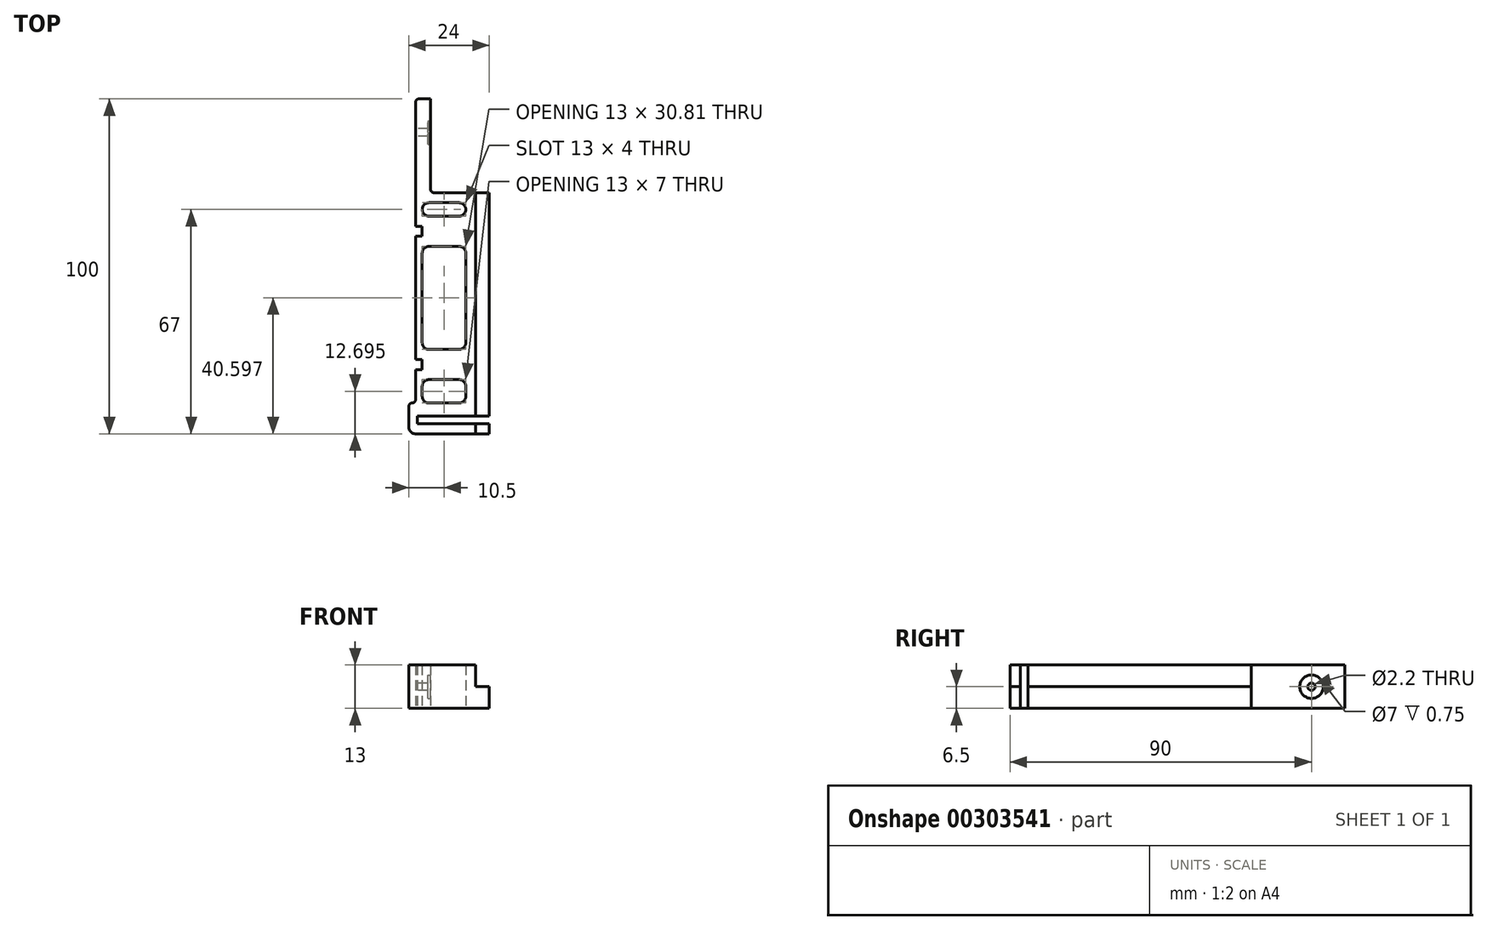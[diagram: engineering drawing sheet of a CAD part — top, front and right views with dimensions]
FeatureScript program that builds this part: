
annotation { "Feature Type Name" : "Feature", "Feature Type Description" : "" }
export const myFeature = defineFeature(function(context is Context, id is Id, definition is map)
    precondition{}
    {
        {
            var Q0;
            Q0=qCreatedBy(makeId("Top.planeOp"),FACE);
            var sketch = newSketch(context, id + "F0", { "sketchPlane" : qUnion([Q0])});
            skLineSegment(sketch, "E0", {"start": v(0, 0) * mm, "end": v(-22, 0) * mm});
            skLineSegment(sketch, "E1", {"start": v(-20, 19.2) * mm, "end": v(-18, 19.2) * mm});
            skLineSegment(sketch, "E2", {"start": v(-18, 19.2) * mm, "end": v(-18, 22.2) * mm});
            skLineSegment(sketch, "E3", {"start": v(-18, 22.2) * mm, "end": v(-20, 22.2) * mm});
            skLineSegment(sketch, "E4", {"start": v(-20, 22.2) * mm, "end": v(-20, 59) * mm});
            skLineSegment(sketch, "E5", {"start": v(-20, 59) * mm, "end": v(-18, 59) * mm});
            skLineSegment(sketch, "E6", {"start": v(-18, 59) * mm, "end": v(-18, 62) * mm});
            skLineSegment(sketch, "E7", {"start": v(-15.5, 100) * mm, "end": v(-15.5, 72) * mm});
            skLineSegment(sketch, "E8", {"start": v(-15.5, 72) * mm, "end": v(0, 72) * mm});
            skLineSegment(sketch, "E9", {"start": v(0, 72) * mm, "end": v(0, 5.3) * mm});
            skLineSegment(sketch, "E10", {"start": v(0, 5.3) * mm, "end": v(-19.5, 5.3) * mm});
            skLineSegment(sketch, "E11", {"start": v(-19.5, 5.3) * mm, "end": v(-19.5, 3) * mm});
            skLineSegment(sketch, "E12", {"start": v(-19.5, 3) * mm, "end": v(0, 3) * mm});
            skLineSegment(sketch, "E13", {"start": v(0, 3) * mm, "end": v(0, 0) * mm});
            skLineSegment(sketch, "E14", {"start": v(-22, 0) * mm, "end": v(-22, 9.2) * mm});
            skLineSegment(sketch, "E15", {"start": v(-18, 62) * mm, "end": v(-20, 62) * mm});
            skLineSegment(sketch, "E16", {"start": v(-20, 62) * mm, "end": v(-20, 100) * mm});
            skLineSegment(sketch, "E17", {"start": v(-20, 100) * mm, "end": v(-15.5, 100) * mm});
            skLineSegment(sketch, "E18", {"start": v(-20, 19.2) * mm, "end": v(-20, 9.2) * mm});
            skLineSegment(sketch, "E19", {"start": v(-20, 9.2) * mm, "end": v(-22, 9.2) * mm});
            skLineSegment(sketch, "E20.bottom", {"start": v(-18, 9.2) * mm, "end": v(-5, 9.2) * mm});
            skLineSegment(sketch, "E20.top", {"start": v(-18, 16.2) * mm, "end": v(-5, 16.2) * mm});
            skLineSegment(sketch, "E20.left", {"start": v(-18, 9.2) * mm, "end": v(-18, 16.2) * mm});
            skLineSegment(sketch, "E20.right", {"start": v(-5, 9.2) * mm, "end": v(-5, 16.2) * mm});
            skLineSegment(sketch, "E21.bottom", {"start": v(-5, 25.2) * mm, "end": v(-18, 25.2) * mm});
            skLineSegment(sketch, "E21.top", {"start": v(-5, 56) * mm, "end": v(-18, 56) * mm});
            skLineSegment(sketch, "E21.left", {"start": v(-5, 25.2) * mm, "end": v(-5, 56) * mm});
            skLineSegment(sketch, "E21.right", {"start": v(-18, 25.2) * mm, "end": v(-18, 56) * mm});
            skLineSegment(sketch, "E22.bottom", {"start": v(-5, 65) * mm, "end": v(-18, 65) * mm});
            skLineSegment(sketch, "E22.top", {"start": v(-5, 69) * mm, "end": v(-18, 69) * mm});
            skLineSegment(sketch, "E22.left", {"start": v(-5, 65) * mm, "end": v(-5, 69) * mm});
            skLineSegment(sketch, "E22.right", {"start": v(-18, 65) * mm, "end": v(-18, 69) * mm});
            skSolve(sketch);
        }
        {
            var Q0;
            Q0=makeQuery(id+"F0.imprint","IMPRINT",FACE,{"disambiguationData":[TD([[makeQuery(id+"F0.imprint","IMPRINT",EDGE,{"derivedFrom":sQuery(id+"F0.wireOp",EDGE,"E0")}),-1.0]])]});
            extrude(context, id + "F1", {"entities" : qUnion([Q0]), "depth" : 13 * mm});
        }
        {
            var Q0;
            Q0=makeQuery(id+"F1.opExtrude","SWEPT_FACE",FACE,{"disambiguationData":[OSD([sQuery(id+"F0.wireOp",EDGE,"E16")])]});
            var sketch = newSketch(context, id + "F2", { "sketchPlane" : qUnion([Q0])});
            skPoint(sketch, "E23", {"position": v(-90, 6.5) * mm});
            skPoint(sketch, "E23.positionSnap0", {"position": v(-100, 6.5) * mm});
            skSolve(sketch);
        }
        {
            var Q0;
            Q0=makeQuery(id+"F1.opExtrude","SWEPT_EDGE",EDGE,{"disambiguationData":[OSD([sQuery(id+"F0.wireOp",EDGE,"E0"),sQuery(id+"F0.wireOp",EDGE,"E14")])]});
            var Q1;
            Q1=makeQuery(id+"F1.opExtrude","SWEPT_EDGE",EDGE,{"disambiguationData":[OSD([sQuery(id+"F0.wireOp",EDGE,"E22.top"),sQuery(id+"F0.wireOp",EDGE,"E22.right")])]});
            var Q2;
            Q2=makeQuery(id+"F1.opExtrude","SWEPT_EDGE",EDGE,{"disambiguationData":[OSD([sQuery(id+"F0.wireOp",EDGE,"E22.bottom"),sQuery(id+"F0.wireOp",EDGE,"E22.right")])]});
            var Q3;
            Q3=makeQuery(id+"F1.opExtrude","SWEPT_EDGE",EDGE,{"disambiguationData":[OSD([sQuery(id+"F0.wireOp",EDGE,"E22.top"),sQuery(id+"F0.wireOp",EDGE,"E22.left")])]});
            var Q4;
            Q4=makeQuery(id+"F1.opExtrude","SWEPT_EDGE",EDGE,{"disambiguationData":[OSD([sQuery(id+"F0.wireOp",EDGE,"E22.bottom"),sQuery(id+"F0.wireOp",EDGE,"E22.left")])]});
            var Q5;
            Q5=makeQuery(id+"F1.opExtrude","SWEPT_EDGE",EDGE,{"disambiguationData":[OSD([sQuery(id+"F0.wireOp",EDGE,"E21.top"),sQuery(id+"F0.wireOp",EDGE,"E21.right")])]});
            var Q6;
            Q6=makeQuery(id+"F1.opExtrude","SWEPT_EDGE",EDGE,{"disambiguationData":[OSD([sQuery(id+"F0.wireOp",EDGE,"E21.top"),sQuery(id+"F0.wireOp",EDGE,"E21.left")])]});
            var Q7;
            Q7=makeQuery(id+"F1.opExtrude","SWEPT_EDGE",EDGE,{"disambiguationData":[OSD([sQuery(id+"F0.wireOp",EDGE,"E21.bottom"),sQuery(id+"F0.wireOp",EDGE,"E21.right")])]});
            var Q8;
            Q8=makeQuery(id+"F1.opExtrude","SWEPT_EDGE",EDGE,{"disambiguationData":[OSD([sQuery(id+"F0.wireOp",EDGE,"E21.bottom"),sQuery(id+"F0.wireOp",EDGE,"E21.left")])]});
            var Q9;
            Q9=makeQuery(id+"F1.opExtrude","SWEPT_EDGE",EDGE,{"disambiguationData":[OSD([sQuery(id+"F0.wireOp",EDGE,"E20.bottom"),sQuery(id+"F0.wireOp",EDGE,"E20.left")])]});
            var Q10;
            Q10=makeQuery(id+"F1.opExtrude","SWEPT_EDGE",EDGE,{"disambiguationData":[OSD([sQuery(id+"F0.wireOp",EDGE,"E20.bottom"),sQuery(id+"F0.wireOp",EDGE,"E20.right")])]});
            var Q11;
            Q11=makeQuery(id+"F1.opExtrude","SWEPT_EDGE",EDGE,{"disambiguationData":[OSD([sQuery(id+"F0.wireOp",EDGE,"E20.top"),sQuery(id+"F0.wireOp",EDGE,"E20.right")])]});
            var Q12;
            Q12=makeQuery(id+"F1.opExtrude","SWEPT_EDGE",EDGE,{"disambiguationData":[OSD([sQuery(id+"F0.wireOp",EDGE,"E20.top"),sQuery(id+"F0.wireOp",EDGE,"E20.left")])]});
            fillet(context, id + "F3", {"entities" : qUnion([Q0, Q1, Q2, Q3, Q4, Q5, Q6, Q7, Q8, Q9, Q10, Q11, Q12]), "radius" : 2 * mm, "tangentPropagation" : true, "allowEdgeOverflow" : false});
        }
        {
            var Q0;
            Q0=makeQuery(id+"F1.opExtrude","SWEPT_EDGE",EDGE,{"disambiguationData":[OSD([sQuery(id+"F0.wireOp",EDGE,"E7"),sQuery(id+"F0.wireOp",EDGE,"E8")])]});
            var Q1;
            Q1=makeQuery(id+"F1.opExtrude","SWEPT_EDGE",EDGE,{"disambiguationData":[OSD([sQuery(id+"F0.wireOp",EDGE,"E16"),sQuery(id+"F0.wireOp",EDGE,"E17")])]});
            var Q2;
            Q2=makeQuery(id+"F1.opExtrude","SWEPT_EDGE",EDGE,{"disambiguationData":[OSD([sQuery(id+"F0.wireOp",EDGE,"E14"),sQuery(id+"F0.wireOp",EDGE,"E19")])]});
            var Q3;
            Q3=makeQuery(id+"F1.opExtrude","SWEPT_EDGE",EDGE,{"disambiguationData":[OSD([sQuery(id+"F0.wireOp",EDGE,"E18"),sQuery(id+"F0.wireOp",EDGE,"E19")])]});
            fillet(context, id + "F4", {"entities" : qUnion([Q0, Q1, Q2, Q3]), "radius" : 1 * mm, "tangentPropagation" : true, "allowEdgeOverflow" : false});
        }
        {
            var Q0;
            Q0=sQuery(id+"F2.wireOp",VERTEX,"E23");
            var Q1;
            Q1=makeQuery(id+"F1.opExtrude","SWEPT_BODY",BODY,{"disambiguationData":[OSD([sQuery(id+"F0.wireOp",EDGE,"E0"),sQuery(id+"F0.wireOp",EDGE,"E1"),sQuery(id+"F0.wireOp",EDGE,"E2"),sQuery(id+"F0.wireOp",EDGE,"E3"),sQuery(id+"F0.wireOp",EDGE,"E4"),sQuery(id+"F0.wireOp",EDGE,"E5"),sQuery(id+"F0.wireOp",EDGE,"E6"),sQuery(id+"F0.wireOp",EDGE,"E7"),sQuery(id+"F0.wireOp",EDGE,"E8"),sQuery(id+"F0.wireOp",EDGE,"E9"),sQuery(id+"F0.wireOp",EDGE,"E10"),sQuery(id+"F0.wireOp",EDGE,"E11"),sQuery(id+"F0.wireOp",EDGE,"E12"),sQuery(id+"F0.wireOp",EDGE,"E13"),sQuery(id+"F0.wireOp",EDGE,"E14"),sQuery(id+"F0.wireOp",EDGE,"E15"),sQuery(id+"F0.wireOp",EDGE,"E16"),sQuery(id+"F0.wireOp",EDGE,"E17"),sQuery(id+"F0.wireOp",EDGE,"E18"),sQuery(id+"F0.wireOp",EDGE,"E19")])]});
            hole(context, id + "F5", {"style" : HoleStyle.SIMPLE, "endStyle" : HoleEndStyle.THROUGH, "holeDiameter" : 2.2 * mm, "tappedDepth" : 12 * mm, "tapClearance" : 3, "locations" : qUnion([Q0]), "scope" : qUnion([Q1])});
        }
        {
            var Q0;
            Q0=makeQuery(id+"F1.opExtrude","SWEPT_FACE",FACE,{"disambiguationData":[OSD([sQuery(id+"F0.wireOp",EDGE,"E9")])]});
            var sketch = newSketch(context, id + "F6", { "sketchPlane" : qUnion([Q0])});
            skLineSegment(sketch, "E24", {"start": v(5.3, 6.5) * mm, "end": v(72, 6.5) * mm});
            skSolve(sketch);
        }
        {
            var Q0;
            Q0=makeQuery(id+"F1.opExtrude","SWEPT_FACE",FACE,{"disambiguationData":[OSD([sQuery(id+"F0.wireOp",EDGE,"E13")])]});
            var sketch = newSketch(context, id + "F7", { "sketchPlane" : qUnion([Q0])});
            skLineSegment(sketch, "E25", {"start": v(3, 6.5) * mm, "end": v(0, 6.5) * mm});
            skSolve(sketch);
        }
        {
            var Q0;
            {var subQ0=sQuery(id+"F7.wireOp",EDGE,"E25");Q0=makeQuery(id+"F7.imprint","IMPRINT",FACE,{"disambiguationData":[TD([[makeQuery(id+"F7.imprint","IMPRINT",EDGE,{"derivedFrom":subQ0}),1.0]])]});}
            var Q1;
            {var subQ0=sQuery(id+"F6.wireOp",EDGE,"E24");Q1=makeQuery(id+"F6.imprint","IMPRINT",FACE,{"disambiguationData":[TD([[makeQuery(id+"F6.imprint","IMPRINT",EDGE,{"derivedFrom":subQ0}),-1.0]])]});}
            extrude(context, id + "F8", {"entities" : qUnion([Q0, Q1]), "operationType" : NewBodyOperationType.ADD, "depth" : 2 * mm});
        }
        {
            var Q0;
            Q0=makeQuery(id+"F1.opExtrude","SWEPT_FACE",FACE,{"disambiguationData":[OSD([sQuery(id+"F0.wireOp",EDGE,"E13")])]});
            var Q1;
            Q1=makeQuery(id+"F1.opExtrude","SWEPT_FACE",FACE,{"disambiguationData":[OSD([sQuery(id+"F0.wireOp",EDGE,"E9")])]});
            extrude(context, id + "F9", {"entities" : qUnion([Q0, Q1]), "operationType" : NewBodyOperationType.REMOVE, "oppositeDirection" : true, "depth" : 2 * mm});
        }
        {
            var Q0;
            Q0=makeQuery(id+"F1.opExtrude","SWEPT_FACE",FACE,{"disambiguationData":[OSD([sQuery(id+"F0.wireOp",EDGE,"E7")])]});
            var sketch = newSketch(context, id + "F10", { "sketchPlane" : qUnion([Q0])});
            skCircle(sketch, "E26", {"center": v(90, 6.5) * mm, "radius": 3.5 * mm});
            skSolve(sketch);
        }
        {
            var Q0;
            Q0=makeQuery(id+"F10.imprint","IMPRINT",FACE,{"disambiguationData":[TD([[makeQuery(id+"F10.imprint","IMPRINT",EDGE,{"derivedFrom":sQuery(id+"F10.wireOp",EDGE,"E26")}),1.0]])]});
            extrude(context, id + "F11", {"entities" : qUnion([Q0]), "operationType" : NewBodyOperationType.REMOVE, "oppositeDirection" : true, "depth" : 0.75 * mm});
        }
    });
